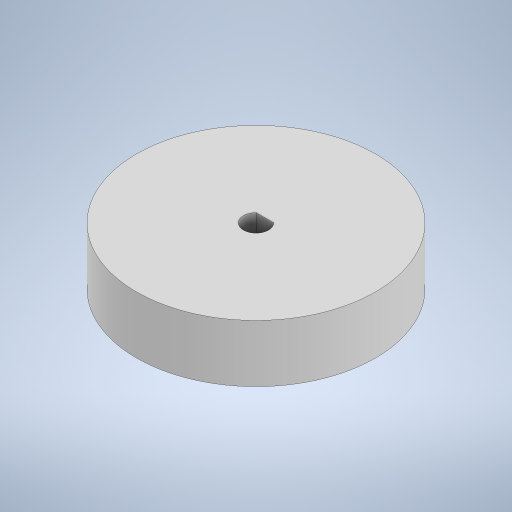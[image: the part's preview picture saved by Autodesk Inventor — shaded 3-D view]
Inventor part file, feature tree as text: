
AUTODESK INVENTOR PART (.ipt)
format: ipt  version: 2023 (Build 270158000, 158)  size: 261,632 bytes
history: native  units: in
note: dims shown in document units (in); Inventor stores cm internally (conversion verified against a paired STEP export)
features: extrude x1, sketch x1
ambient origin geometry x8: Origin, YZ Plane, XZ Plane, XY Plane, X Axis, Y Axis, Z Axis, Center Point
bodies: Body1 (feature_tree)
feature tree (2):
  extrude  "Extrusion2"  Depth=0.4724in
  sketch  "Sketch1"  dims[d0=1.9685in d1=0.2067in d2=0.1772in d22=5.9055in d24=360.0deg d26=0.4724in d27=0.0in]
